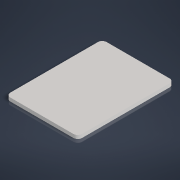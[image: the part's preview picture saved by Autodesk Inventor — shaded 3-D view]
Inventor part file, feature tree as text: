
AUTODESK INVENTOR PART (.ipt)
format: ipt  version: 2022 (Build 260153070, 153G)  size: 95,232 bytes
history: native  units: mm
features: other x1, extrude x1, sketch x1
ambient origin geometry x8: Origin, YZ Plane, XZ Plane, XY Plane, X Axis, Y Axis, Z Axis, Center Point
bodies: Body1 (feature_tree)
feature tree (3):
  other  "Твердое тело1"
  extrude  "Выдавливание1"  Depth=2.0mm
  sketch  "Эскиз1"
